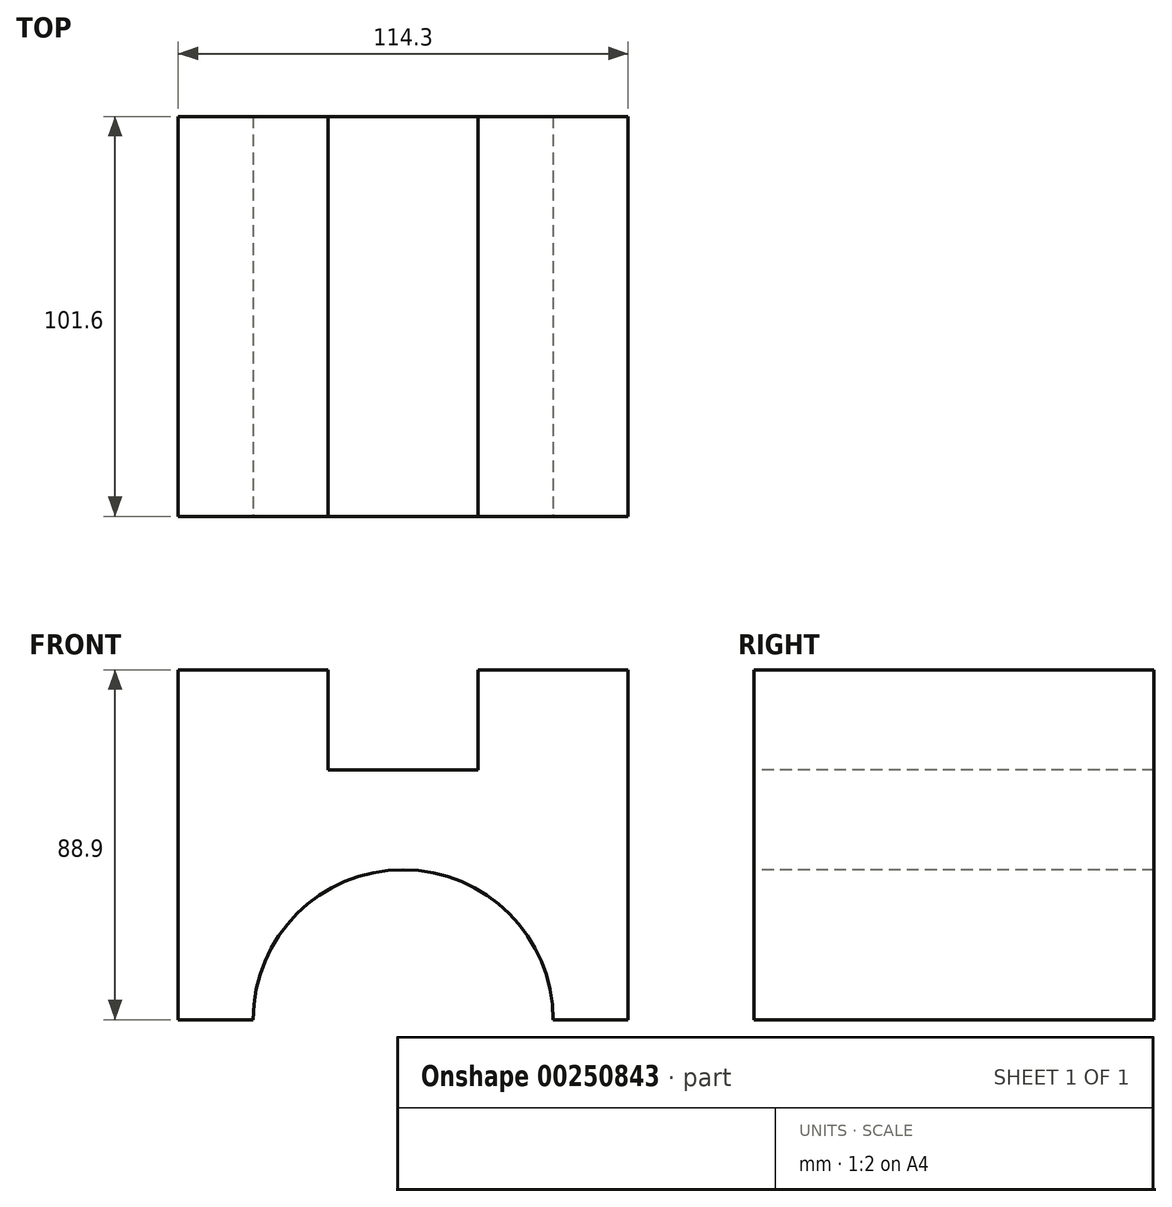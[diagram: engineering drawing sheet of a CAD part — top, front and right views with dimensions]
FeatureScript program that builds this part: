
annotation { "Feature Type Name" : "Feature", "Feature Type Description" : "" }
export const myFeature = defineFeature(function(context is Context, id is Id, definition is map)
    precondition{}
    {
        {
            var Q0;
            Q0=qCreatedBy(makeId("Top.planeOp"),FACE);
            var sketch = newSketch(context, id + "F0", { "sketchPlane" : qUnion([Q0])});
            skLineSegment(sketch, "E0.bottom", {"start": v(0, 0) * mm, "end": v(114.3, 0) * mm});
            skLineSegment(sketch, "E0.top", {"start": v(0, 101.6) * mm, "end": v(114.3, 101.6) * mm});
            skLineSegment(sketch, "E0.left", {"start": v(0, 0) * mm, "end": v(0, 101.6) * mm});
            skLineSegment(sketch, "E0.right", {"start": v(114.3, 0) * mm, "end": v(114.3, 101.6) * mm});
            skSolve(sketch);
        }
        {
            var Q0;
            Q0=makeQuery(id+"F0.imprint","IMPRINT",FACE,{"disambiguationData":[TD([[makeQuery(id+"F0.imprint","IMPRINT",EDGE,{"derivedFrom":sQuery(id+"F0.wireOp",EDGE,"E0.bottom")}),1.0]])]});
            extrude(context, id + "F1", {"entities" : qUnion([Q0]), "depth" : 63.5 * mm});
        }
        {
            var Q0;
            Q0=makeQuery(id+"F1.opExtrude","CAP_FACE",FACE,{"disambiguationData":[OSD([sQuery(id+"F0.wireOp",EDGE,"E0.bottom"),sQuery(id+"F0.wireOp",EDGE,"E0.top"),sQuery(id+"F0.wireOp",EDGE,"E0.left"),sQuery(id+"F0.wireOp",EDGE,"E0.right")])],"isStart":false});
            var sketch = newSketch(context, id + "F2", { "sketchPlane" : qUnion([Q0])});
            skLineSegment(sketch, "E1.bottom", {"start": v(0, 101.6) * mm, "end": v(38.1, 101.6) * mm});
            skLineSegment(sketch, "E1.top", {"start": v(0, 0) * mm, "end": v(38.1, 0) * mm});
            skLineSegment(sketch, "E1.left", {"start": v(0, 101.6) * mm, "end": v(0, 0) * mm});
            skLineSegment(sketch, "E1.right", {"start": v(38.1, 101.6) * mm, "end": v(38.1, 0) * mm});
            skLineSegment(sketch, "E2.bottom", {"start": v(114.3, 101.6) * mm, "end": v(76.2, 101.6) * mm});
            skLineSegment(sketch, "E2.top", {"start": v(114.3, 0) * mm, "end": v(76.2, 0) * mm});
            skLineSegment(sketch, "E2.left", {"start": v(114.3, 101.6) * mm, "end": v(114.3, 0) * mm});
            skLineSegment(sketch, "E2.right", {"start": v(76.2, 101.6) * mm, "end": v(76.2, 0) * mm});
            skSolve(sketch);
        }
        {
            var Q0;
            Q0=makeQuery(id+"F2.imprint","IMPRINT",FACE,{"disambiguationData":[TD([[makeQuery(id+"F2.imprint","IMPRINT",EDGE,{"derivedFrom":sQuery(id+"F2.wireOp",EDGE,"E1.bottom")}),-1.0]])]});
            var Q1;
            Q1=makeQuery(id+"F2.imprint","IMPRINT",FACE,{"disambiguationData":[TD([[makeQuery(id+"F2.imprint","IMPRINT",EDGE,{"derivedFrom":sQuery(id+"F2.wireOp",EDGE,"E2.bottom")}),-1.0]])]});
            extrude(context, id + "F3", {"entities" : qUnion([Q0, Q1]), "operationType" : NewBodyOperationType.ADD, "depth" : 25.4 * mm});
        }
        {
            var Q0;
            Q0=makeQuery(id+"F3.boolean.opBoolean","MERGE",FACE,{"derivedFrom":[makeQuery(id+"F1.opExtrude","SWEPT_FACE",FACE,{"disambiguationData":[OSD([sQuery(id+"F0.wireOp",EDGE,"E0.bottom")])]}),makeQuery(id+"F3.opExtrude","SWEPT_FACE",FACE,{"disambiguationData":[OSD([sQuery(id+"F2.wireOp",EDGE,"E1.top")])]}),makeQuery(id+"F3.opExtrude","SWEPT_FACE",FACE,{"disambiguationData":[OSD([sQuery(id+"F2.wireOp",EDGE,"E2.top")])]})]});
            var sketch = newSketch(context, id + "F4", { "sketchPlane" : qUnion([Q0])});
            skPoint(sketch, "E3", {"position": v(57.15, 0) * mm});
            skSolve(sketch);
        }
        {
            var Q0;
            Q0=sQuery(id+"F4.wireOp",VERTEX,"E3");
            var Q1;
            Q1=makeQuery(id+"F1.opExtrude","SWEPT_BODY",BODY,{"disambiguationData":[OSD([sQuery(id+"F0.wireOp",EDGE,"E0.bottom"),sQuery(id+"F0.wireOp",EDGE,"E0.top"),sQuery(id+"F0.wireOp",EDGE,"E0.left"),sQuery(id+"F0.wireOp",EDGE,"E0.right")])]});
            hole(context, id + "F5", {"style" : HoleStyle.SIMPLE, "endStyle" : HoleEndStyle.THROUGH, "holeDiameter" : 76.2 * mm, "tappedDepth" : 12.7 * mm, "tapClearance" : 3, "locations" : qUnion([Q0]), "scope" : qUnion([Q1])});
        }
    });
